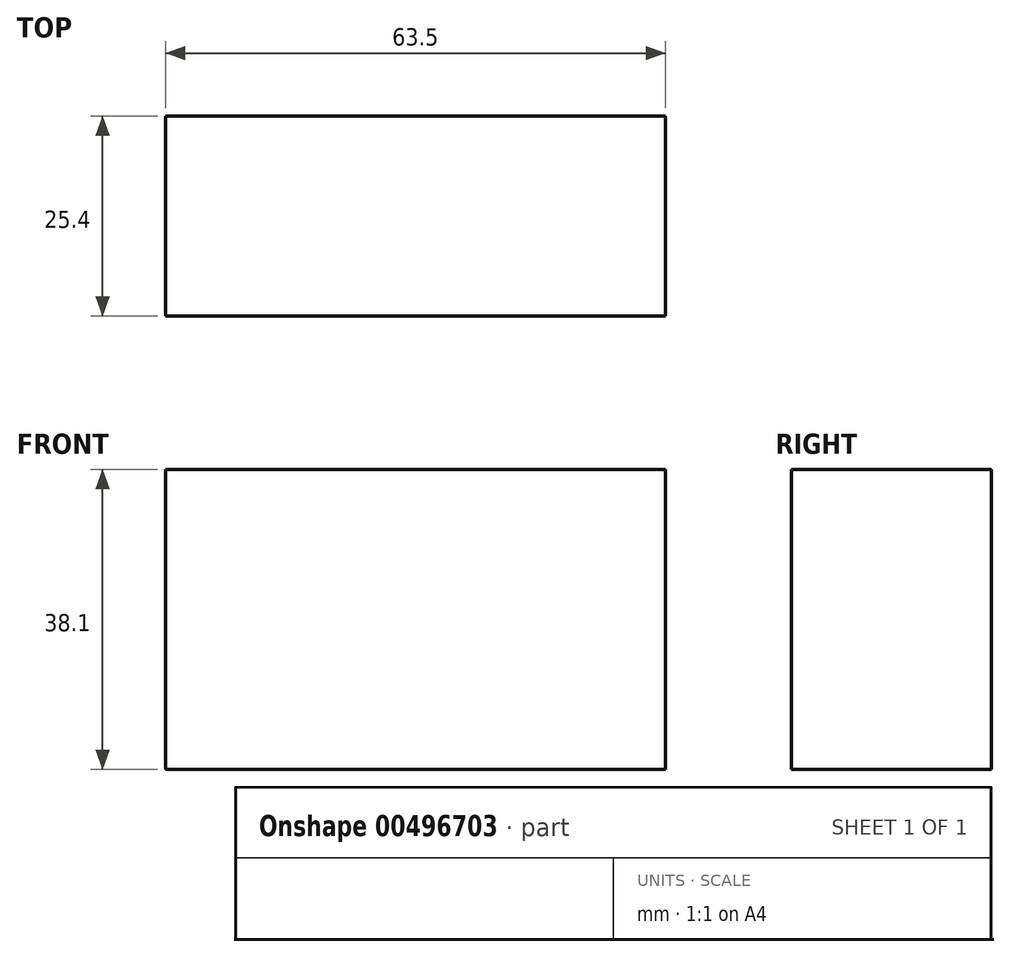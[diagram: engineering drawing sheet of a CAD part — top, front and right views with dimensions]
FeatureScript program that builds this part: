
annotation { "Feature Type Name" : "Feature", "Feature Type Description" : "" }
export const myFeature = defineFeature(function(context is Context, id is Id, definition is map)
    precondition{}
    {
        {
            var Q0;
            Q0=qCreatedBy(makeId("Front.planeOp"),FACE);
            var sketch = newSketch(context, id + "F0", { "sketchPlane" : qUnion([Q0])});
            skLineSegment(sketch, "E0.bottom", {"start": v(-55.99, 29.55) * mm, "end": v(7.51, 29.55) * mm});
            skLineSegment(sketch, "E0.top", {"start": v(-55.99, -8.55) * mm, "end": v(7.51, -8.55) * mm});
            skLineSegment(sketch, "E0.left", {"start": v(-55.99, 29.55) * mm, "end": v(-55.99, -8.55) * mm});
            skLineSegment(sketch, "E0.right", {"start": v(7.51, 29.55) * mm, "end": v(7.51, -8.55) * mm});
            skSolve(sketch);
        }
        {
            var Q0;
            Q0=makeQuery(id+"F0.imprint","IMPRINT",FACE,{"disambiguationData":[TD([[makeQuery(id+"F0.imprint","IMPRINT",EDGE,{"derivedFrom":sQuery(id+"F0.wireOp",EDGE,"E0.bottom")}),-1.0]])]});
            extrude(context, id + "F1", {"entities" : qUnion([Q0]), "depth" : 25.4 * mm});
        }
    });
